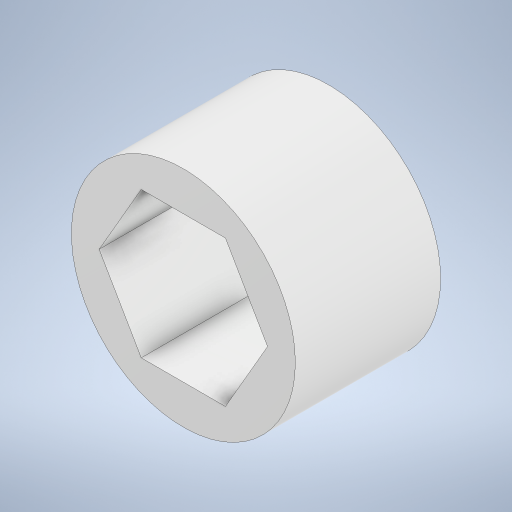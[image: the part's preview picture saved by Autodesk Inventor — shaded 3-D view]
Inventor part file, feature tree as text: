
AUTODESK INVENTOR PART (.ipt)
format: ipt  version: 2024 (Build 280153000, 153)  size: 221,696 bytes
history: native  units: in
note: dims shown in document units (in); Inventor stores cm internally (conversion verified against a paired STEP export)
features: extrude x1, sketch x1
ambient origin geometry x8: Origin, YZ Plane, XZ Plane, XY Plane, X Axis, Y Axis, Z Axis, Center Point
bodies: Solid1 (feature_tree)
feature tree (2):
  extrude  "Extrusion1"  Depth=0.5in
  sketch  "Sketch1"  dims[d0=0.7677in d1=0.5in d2=0.498in d3=0.0in]
